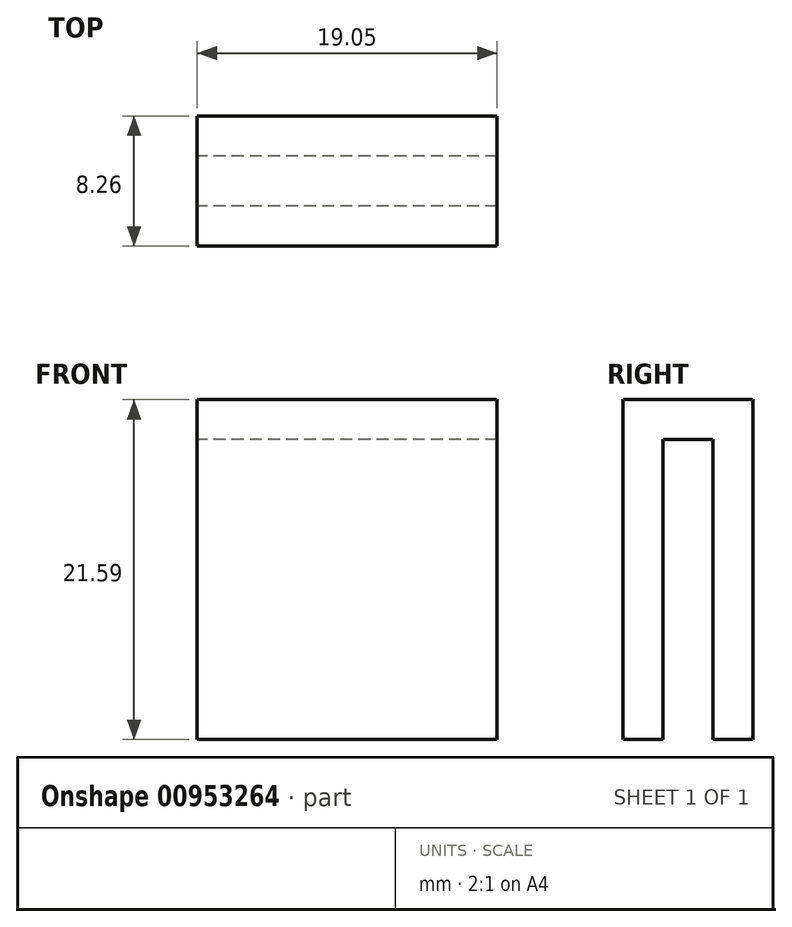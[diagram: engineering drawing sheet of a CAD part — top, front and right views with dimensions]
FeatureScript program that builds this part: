
annotation { "Feature Type Name" : "Feature", "Feature Type Description" : "" }
export const myFeature = defineFeature(function(context is Context, id is Id, definition is map)
    precondition{}
    {
        {
            var Q0;
            Q0=qCreatedBy(makeId("Right.planeOp"),FACE);
            var sketch = newSketch(context, id + "F0", { "sketchPlane" : qUnion([Q0])});
            skLineSegment(sketch, "E0.bottom", {"start": v(-4.13, 21.59) * mm, "end": v(4.13, 21.59) * mm});
            skLineSegment(sketch, "E0.top", {"start": v(-4.13, 0) * mm, "end": v(-1.59, 0) * mm});
            skLineSegment(sketch, "E0.left", {"start": v(-4.13, 21.59) * mm, "end": v(-4.13, 0) * mm});
            skLineSegment(sketch, "E0.right", {"start": v(4.13, 21.59) * mm, "end": v(4.13, 0) * mm});
            skLineSegment(sketch, "E1.top", {"start": v(1.59, 19.05) * mm, "end": v(-1.59, 19.05) * mm});
            skLineSegment(sketch, "E1.left", {"start": v(1.59, 0) * mm, "end": v(1.59, 19.05) * mm});
            skLineSegment(sketch, "E1.right", {"start": v(-1.59, 0) * mm, "end": v(-1.59, 19.05) * mm});
            skPoint(sketch, "E2", {"position": v(0, 19.05) * mm});
            skPoint(sketch, "E3", {"position": v(0, 21.59) * mm});
            skLineSegment(sketch, "E4.trimOffspring", {"start": v(1.59, 0) * mm, "end": v(4.13, 0) * mm});
            skSolve(sketch);
        }
        {
            var Q0;
            Q0=qSketchRegion(id+"F0",true);
            extrude(context, id + "F1", {"entities" : qUnion([Q0]), "depth" : 19.05 * mm, "offsetDistance" : 25.4 * mm});
        }
    });
